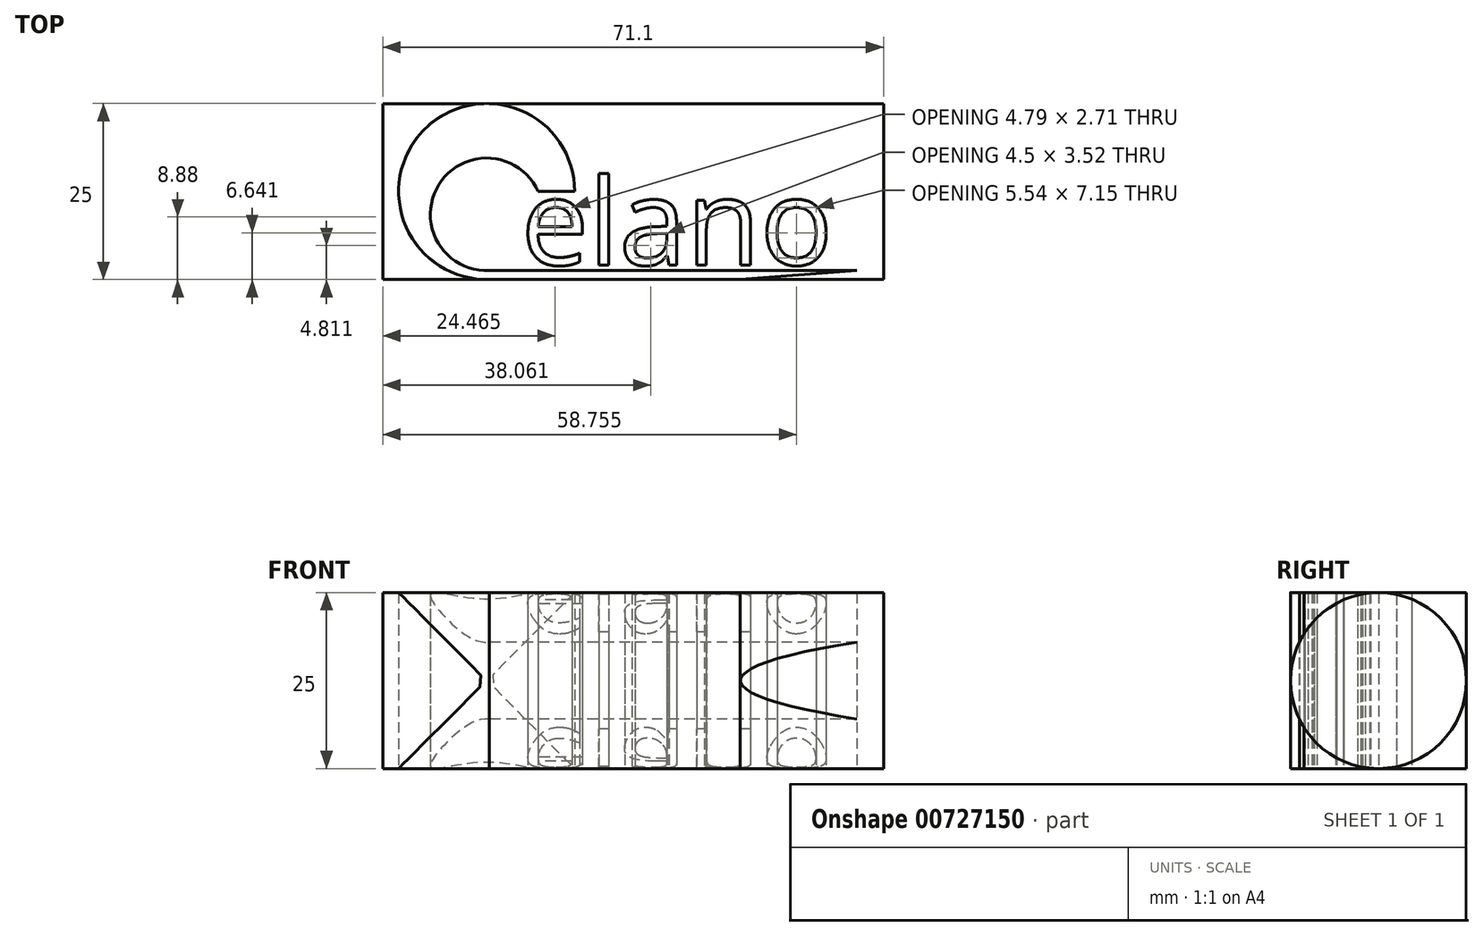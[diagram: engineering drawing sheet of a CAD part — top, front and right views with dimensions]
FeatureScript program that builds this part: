
annotation { "Feature Type Name" : "Feature", "Feature Type Description" : "" }
export const myFeature = defineFeature(function(context is Context, id is Id, definition is map)
    precondition{}
    {
        {
            var Q0;
            Q0=qCreatedBy(makeId("Top.planeOp"),FACE);
            var sketch = newSketch(context, id + "F0", { "sketchPlane" : qUnion([Q0])});
            skArc(sketch, "E0", {"start": v(-21.85, 0) * mm, "mid": v(-43.32, 8.7) * mm, "end": v(-33.99, -12.5) * mm});
            skLineSegment(sketch, "E1", {"start": v(-33.99, -12.5) * mm, "end": v(1.63, -12.5) * mm});
            skArc(sketch, "E2", {"start": v(-27.04, 0) * mm, "mid": v(-41.16, 0.95) * mm, "end": v(-33.99, -11.24) * mm});
            skLineSegment(sketch, "E3", {"start": v(-27.04, 0) * mm, "end": v(-21.85, 0) * mm});
            skLineSegment(sketch, "E4", {"start": v(-33.99, -11.24) * mm, "end": v(18.22, -11.24) * mm});
            skLineSegment(sketch, "E5", {"start": v(18.22, -11.24) * mm, "end": v(1.63, -12.5) * mm});
            skPoint(sketch, "E6.orphan", {"position": v(70.43, -11.24) * mm});
            skPoint(sketch, "E7.orphan", {"position": v(44.57, -12.5) * mm});
            skText(sketch, "E8", { "text": "elano", "fontName": "OpenSans-Regular.ttf"});
            const initialGuessF0  = {"E8": [-0.02946, -0.01043, 1, 0, 0.01232]};
            skSetInitialGuess(sketch, initialGuessF0);
            skSolve(sketch);
        }
        {
            var Q0;
            Q0 = qSketchRegion(id + "F0", true);
            extrude(context, id + "F1", {"entities" : qUnion([Q0]), "depth" : 25 * mm, "offsetDistance" : 25 * mm});
        }
        {
            var Q0;
            Q0=qCreatedBy(makeId("Right.planeOp"),FACE);
            var sketch = newSketch(context, id + "F2", { "sketchPlane" : qUnion([Q0])});
            skLineSegment(sketch, "E9", {"start": v(12.5, 25) * mm, "end": v(12.5, 0) * mm});
            skLineSegment(sketch, "E10.0", {"start": v(-12.5, 25) * mm, "end": v(12.5, 25) * mm});
            skLineSegment(sketch, "E11.0", {"start": v(-12.5, 25) * mm, "end": v(-12.5, 0) * mm});
            skLineSegment(sketch, "E12", {"start": v(-12.5, 0) * mm, "end": v(-12.5, 25) * mm});
            skCircle(sketch, "E13", {"center": v(0, 12.5) * mm, "radius": 12.5 * mm});
            skPoint(sketch, "E13.centerSnap0", {"position": v(-12.5, 12.5) * mm});
            skSolve(sketch);
        }
        {
            var Q0;
            Q0 = qSketchRegion(id + "F2", true);
            extrude(context, id + "F3", {"entities" : qUnion([Q0]), "depth" : 22 * mm, "offsetDistance" : 25 * mm, "hasSecondDirection" : true, "secondDirectionOppositeDirection" : true, "secondDirectionDepth" : 49.1 * mm});
        }
        {
            var Q0;
            Q0=makeQuery(id+"F3.opExtrude","SWEPT_BODY",BODY,{"disambiguationData":[OSD([sQuery(id+"F2.wireOp",EDGE,"E13")])]});
            var Q1;
            Q1=makeQuery(id+"F1.opExtrude","SWEPT_BODY",BODY,{"disambiguationData":[OSD([sQuery(id+"F0.wireOp",EDGE,"E8.sketch_text.stroke-67"),sQuery(id+"F0.wireOp",EDGE,"E8.sketch_text.stroke-68"),sQuery(id+"F0.wireOp",EDGE,"E8.sketch_text.stroke-69"),sQuery(id+"F0.wireOp",EDGE,"E8.sketch_text.stroke-70"),sQuery(id+"F0.wireOp",EDGE,"E8.sketch_text.stroke-71"),sQuery(id+"F0.wireOp",EDGE,"E8.sketch_text.stroke-72"),sQuery(id+"F0.wireOp",EDGE,"E8.sketch_text.stroke-73"),sQuery(id+"F0.wireOp",EDGE,"E8.sketch_text.stroke-74"),sQuery(id+"F0.wireOp",EDGE,"E8.sketch_text.stroke-75"),sQuery(id+"F0.wireOp",EDGE,"E8.sketch_text.stroke-76"),sQuery(id+"F0.wireOp",EDGE,"E8.sketch_text.stroke-77"),sQuery(id+"F0.wireOp",EDGE,"E8.sketch_text.stroke-78"),sQuery(id+"F0.wireOp",EDGE,"E8.sketch_text.stroke-79"),sQuery(id+"F0.wireOp",EDGE,"E8.sketch_text.stroke-80"),sQuery(id+"F0.wireOp",EDGE,"E8.sketch_text.stroke-81"),sQuery(id+"F0.wireOp",EDGE,"E8.sketch_text.stroke-82"),sQuery(id+"F0.wireOp",EDGE,"E8.sketch_text.stroke-83")])]});
            var Q2;
            Q2=makeQuery(id+"F1.opExtrude","SWEPT_BODY",BODY,{"disambiguationData":[OSD([sQuery(id+"F0.wireOp",EDGE,"E8.sketch_text.stroke-50"),sQuery(id+"F0.wireOp",EDGE,"E8.sketch_text.stroke-51"),sQuery(id+"F0.wireOp",EDGE,"E8.sketch_text.stroke-52"),sQuery(id+"F0.wireOp",EDGE,"E8.sketch_text.stroke-53"),sQuery(id+"F0.wireOp",EDGE,"E8.sketch_text.stroke-54"),sQuery(id+"F0.wireOp",EDGE,"E8.sketch_text.stroke-55"),sQuery(id+"F0.wireOp",EDGE,"E8.sketch_text.stroke-56"),sQuery(id+"F0.wireOp",EDGE,"E8.sketch_text.stroke-57"),sQuery(id+"F0.wireOp",EDGE,"E8.sketch_text.stroke-58"),sQuery(id+"F0.wireOp",EDGE,"E8.sketch_text.stroke-59"),sQuery(id+"F0.wireOp",EDGE,"E8.sketch_text.stroke-60"),sQuery(id+"F0.wireOp",EDGE,"E8.sketch_text.stroke-61"),sQuery(id+"F0.wireOp",EDGE,"E8.sketch_text.stroke-62"),sQuery(id+"F0.wireOp",EDGE,"E8.sketch_text.stroke-63"),sQuery(id+"F0.wireOp",EDGE,"E8.sketch_text.stroke-64"),sQuery(id+"F0.wireOp",EDGE,"E8.sketch_text.stroke-65"),sQuery(id+"F0.wireOp",EDGE,"E8.sketch_text.stroke-66")])]});
            var Q3;
            Q3=makeQuery(id+"F1.opExtrude","SWEPT_BODY",BODY,{"disambiguationData":[OSD([sQuery(id+"F0.wireOp",EDGE,"E8.sketch_text.stroke-23"),sQuery(id+"F0.wireOp",EDGE,"E8.sketch_text.stroke-24"),sQuery(id+"F0.wireOp",EDGE,"E8.sketch_text.stroke-25"),sQuery(id+"F0.wireOp",EDGE,"E8.sketch_text.stroke-26"),sQuery(id+"F0.wireOp",EDGE,"E8.sketch_text.stroke-27"),sQuery(id+"F0.wireOp",EDGE,"E8.sketch_text.stroke-28"),sQuery(id+"F0.wireOp",EDGE,"E8.sketch_text.stroke-29"),sQuery(id+"F0.wireOp",EDGE,"E8.sketch_text.stroke-30"),sQuery(id+"F0.wireOp",EDGE,"E8.sketch_text.stroke-31"),sQuery(id+"F0.wireOp",EDGE,"E8.sketch_text.stroke-32"),sQuery(id+"F0.wireOp",EDGE,"E8.sketch_text.stroke-33"),sQuery(id+"F0.wireOp",EDGE,"E8.sketch_text.stroke-34"),sQuery(id+"F0.wireOp",EDGE,"E8.sketch_text.stroke-35"),sQuery(id+"F0.wireOp",EDGE,"E8.sketch_text.stroke-36"),sQuery(id+"F0.wireOp",EDGE,"E8.sketch_text.stroke-37"),sQuery(id+"F0.wireOp",EDGE,"E8.sketch_text.stroke-38"),sQuery(id+"F0.wireOp",EDGE,"E8.sketch_text.stroke-39"),sQuery(id+"F0.wireOp",EDGE,"E8.sketch_text.stroke-40"),sQuery(id+"F0.wireOp",EDGE,"E8.sketch_text.stroke-41"),sQuery(id+"F0.wireOp",EDGE,"E8.sketch_text.stroke-42"),sQuery(id+"F0.wireOp",EDGE,"E8.sketch_text.stroke-43"),sQuery(id+"F0.wireOp",EDGE,"E8.sketch_text.stroke-44"),sQuery(id+"F0.wireOp",EDGE,"E8.sketch_text.stroke-45"),sQuery(id+"F0.wireOp",EDGE,"E8.sketch_text.stroke-46"),sQuery(id+"F0.wireOp",EDGE,"E8.sketch_text.stroke-47"),sQuery(id+"F0.wireOp",EDGE,"E8.sketch_text.stroke-48"),sQuery(id+"F0.wireOp",EDGE,"E8.sketch_text.stroke-49")])]});
            var Q4;
            Q4=makeQuery(id+"F1.opExtrude","SWEPT_BODY",BODY,{"disambiguationData":[OSD([sQuery(id+"F0.wireOp",EDGE,"E8.sketch_text.stroke-0"),sQuery(id+"F0.wireOp",EDGE,"E8.sketch_text.stroke-1"),sQuery(id+"F0.wireOp",EDGE,"E8.sketch_text.stroke-2"),sQuery(id+"F0.wireOp",EDGE,"E8.sketch_text.stroke-3"),sQuery(id+"F0.wireOp",EDGE,"E8.sketch_text.stroke-4"),sQuery(id+"F0.wireOp",EDGE,"E8.sketch_text.stroke-5"),sQuery(id+"F0.wireOp",EDGE,"E8.sketch_text.stroke-6"),sQuery(id+"F0.wireOp",EDGE,"E8.sketch_text.stroke-7"),sQuery(id+"F0.wireOp",EDGE,"E8.sketch_text.stroke-8"),sQuery(id+"F0.wireOp",EDGE,"E8.sketch_text.stroke-9"),sQuery(id+"F0.wireOp",EDGE,"E8.sketch_text.stroke-10"),sQuery(id+"F0.wireOp",EDGE,"E8.sketch_text.stroke-11"),sQuery(id+"F0.wireOp",EDGE,"E8.sketch_text.stroke-12"),sQuery(id+"F0.wireOp",EDGE,"E8.sketch_text.stroke-13"),sQuery(id+"F0.wireOp",EDGE,"E8.sketch_text.stroke-14"),sQuery(id+"F0.wireOp",EDGE,"E8.sketch_text.stroke-15"),sQuery(id+"F0.wireOp",EDGE,"E8.sketch_text.stroke-16"),sQuery(id+"F0.wireOp",EDGE,"E8.sketch_text.stroke-17"),sQuery(id+"F0.wireOp",EDGE,"E8.sketch_text.stroke-18")])]});
            var Q5;
            Q5=makeQuery(id+"F1.opExtrude","SWEPT_BODY",BODY,{"disambiguationData":[OSD([sQuery(id+"F0.wireOp",EDGE,"E0"),sQuery(id+"F0.wireOp",EDGE,"E1"),sQuery(id+"F0.wireOp",EDGE,"E2"),sQuery(id+"F0.wireOp",EDGE,"E3"),sQuery(id+"F0.wireOp",EDGE,"E4"),sQuery(id+"F0.wireOp",EDGE,"E5")])]});
            var Q6;
            Q6=makeQuery(id+"F1.opExtrude","SWEPT_BODY",BODY,{"disambiguationData":[OSD([sQuery(id+"F0.wireOp",EDGE,"E8.sketch_text.stroke-19"),sQuery(id+"F0.wireOp",EDGE,"E8.sketch_text.stroke-20"),sQuery(id+"F0.wireOp",EDGE,"E8.sketch_text.stroke-21"),sQuery(id+"F0.wireOp",EDGE,"E8.sketch_text.stroke-22")])]});
            booleanBodies(context, id + "F4", {"operationType" : BooleanOperationType.INTERSECTION, "tools" : qUnion([Q0, Q1, Q2, Q3, Q4, Q5, Q6]), "keepTools" : true});
        }
        {
            var Q0;
            Q0=makeQuery(id+"F3.opExtrude","SWEPT_BODY",BODY,{"disambiguationData":[OSD([sQuery(id+"F2.wireOp",EDGE,"E13")])]});
            var Q1;
            Q1=makeQuery(id+"F1.opExtrude","SWEPT_BODY",BODY,{"disambiguationData":[OSD([sQuery(id+"F0.wireOp",EDGE,"E0"),sQuery(id+"F0.wireOp",EDGE,"E1"),sQuery(id+"F0.wireOp",EDGE,"E2"),sQuery(id+"F0.wireOp",EDGE,"E3"),sQuery(id+"F0.wireOp",EDGE,"E4"),sQuery(id+"F0.wireOp",EDGE,"E5")])]});
            booleanBodies(context, id + "F5", {"operationType" : BooleanOperationType.INTERSECTION, "tools" : qUnion([Q0, Q1]), "keepTools" : true});
        }
        {
            var Q0;
            Q0=makeQuery(id+"F3.opExtrude","SWEPT_BODY",BODY,{"disambiguationData":[OSD([sQuery(id+"F2.wireOp",EDGE,"E13")])]});
            var Q1;
            Q1=makeQuery(id+"F1.opExtrude","SWEPT_BODY",BODY,{"disambiguationData":[OSD([sQuery(id+"F0.wireOp",EDGE,"E8.sketch_text.stroke-0"),sQuery(id+"F0.wireOp",EDGE,"E8.sketch_text.stroke-1"),sQuery(id+"F0.wireOp",EDGE,"E8.sketch_text.stroke-2"),sQuery(id+"F0.wireOp",EDGE,"E8.sketch_text.stroke-3"),sQuery(id+"F0.wireOp",EDGE,"E8.sketch_text.stroke-4"),sQuery(id+"F0.wireOp",EDGE,"E8.sketch_text.stroke-5"),sQuery(id+"F0.wireOp",EDGE,"E8.sketch_text.stroke-6"),sQuery(id+"F0.wireOp",EDGE,"E8.sketch_text.stroke-7"),sQuery(id+"F0.wireOp",EDGE,"E8.sketch_text.stroke-8"),sQuery(id+"F0.wireOp",EDGE,"E8.sketch_text.stroke-9"),sQuery(id+"F0.wireOp",EDGE,"E8.sketch_text.stroke-10"),sQuery(id+"F0.wireOp",EDGE,"E8.sketch_text.stroke-11"),sQuery(id+"F0.wireOp",EDGE,"E8.sketch_text.stroke-12"),sQuery(id+"F0.wireOp",EDGE,"E8.sketch_text.stroke-13"),sQuery(id+"F0.wireOp",EDGE,"E8.sketch_text.stroke-14"),sQuery(id+"F0.wireOp",EDGE,"E8.sketch_text.stroke-15"),sQuery(id+"F0.wireOp",EDGE,"E8.sketch_text.stroke-16"),sQuery(id+"F0.wireOp",EDGE,"E8.sketch_text.stroke-17"),sQuery(id+"F0.wireOp",EDGE,"E8.sketch_text.stroke-18")])]});
            booleanBodies(context, id + "F6", {"operationType" : BooleanOperationType.INTERSECTION, "tools" : qUnion([Q0, Q1]), "keepTools" : true});
        }
        {
            var Q0;
            Q0=makeQuery(id+"F3.opExtrude","SWEPT_BODY",BODY,{"disambiguationData":[OSD([sQuery(id+"F2.wireOp",EDGE,"E13")])]});
            var Q1;
            Q1=makeQuery(id+"F1.opExtrude","SWEPT_BODY",BODY,{"disambiguationData":[OSD([sQuery(id+"F0.wireOp",EDGE,"E8.sketch_text.stroke-19"),sQuery(id+"F0.wireOp",EDGE,"E8.sketch_text.stroke-20"),sQuery(id+"F0.wireOp",EDGE,"E8.sketch_text.stroke-21"),sQuery(id+"F0.wireOp",EDGE,"E8.sketch_text.stroke-22")])]});
            booleanBodies(context, id + "F7", {"operationType" : BooleanOperationType.INTERSECTION, "tools" : qUnion([Q0, Q1]), "keepTools" : true});
        }
        {
            var Q0;
            Q0=makeQuery(id+"F3.opExtrude","SWEPT_BODY",BODY,{"disambiguationData":[OSD([sQuery(id+"F2.wireOp",EDGE,"E13")])]});
            var Q1;
            Q1=makeQuery(id+"F1.opExtrude","SWEPT_BODY",BODY,{"disambiguationData":[OSD([sQuery(id+"F0.wireOp",EDGE,"E8.sketch_text.stroke-23"),sQuery(id+"F0.wireOp",EDGE,"E8.sketch_text.stroke-24"),sQuery(id+"F0.wireOp",EDGE,"E8.sketch_text.stroke-25"),sQuery(id+"F0.wireOp",EDGE,"E8.sketch_text.stroke-26"),sQuery(id+"F0.wireOp",EDGE,"E8.sketch_text.stroke-27"),sQuery(id+"F0.wireOp",EDGE,"E8.sketch_text.stroke-28"),sQuery(id+"F0.wireOp",EDGE,"E8.sketch_text.stroke-29"),sQuery(id+"F0.wireOp",EDGE,"E8.sketch_text.stroke-30"),sQuery(id+"F0.wireOp",EDGE,"E8.sketch_text.stroke-31"),sQuery(id+"F0.wireOp",EDGE,"E8.sketch_text.stroke-32"),sQuery(id+"F0.wireOp",EDGE,"E8.sketch_text.stroke-33"),sQuery(id+"F0.wireOp",EDGE,"E8.sketch_text.stroke-34"),sQuery(id+"F0.wireOp",EDGE,"E8.sketch_text.stroke-35"),sQuery(id+"F0.wireOp",EDGE,"E8.sketch_text.stroke-36"),sQuery(id+"F0.wireOp",EDGE,"E8.sketch_text.stroke-37"),sQuery(id+"F0.wireOp",EDGE,"E8.sketch_text.stroke-38"),sQuery(id+"F0.wireOp",EDGE,"E8.sketch_text.stroke-39"),sQuery(id+"F0.wireOp",EDGE,"E8.sketch_text.stroke-40"),sQuery(id+"F0.wireOp",EDGE,"E8.sketch_text.stroke-41"),sQuery(id+"F0.wireOp",EDGE,"E8.sketch_text.stroke-42"),sQuery(id+"F0.wireOp",EDGE,"E8.sketch_text.stroke-43"),sQuery(id+"F0.wireOp",EDGE,"E8.sketch_text.stroke-44"),sQuery(id+"F0.wireOp",EDGE,"E8.sketch_text.stroke-45"),sQuery(id+"F0.wireOp",EDGE,"E8.sketch_text.stroke-46"),sQuery(id+"F0.wireOp",EDGE,"E8.sketch_text.stroke-47"),sQuery(id+"F0.wireOp",EDGE,"E8.sketch_text.stroke-48"),sQuery(id+"F0.wireOp",EDGE,"E8.sketch_text.stroke-49")])]});
            booleanBodies(context, id + "F8", {"operationType" : BooleanOperationType.INTERSECTION, "tools" : qUnion([Q0, Q1]), "keepTools" : true});
        }
        {
            var Q0;
            Q0=makeQuery(id+"F3.opExtrude","SWEPT_BODY",BODY,{"disambiguationData":[OSD([sQuery(id+"F2.wireOp",EDGE,"E13")])]});
            var Q1;
            Q1=makeQuery(id+"F1.opExtrude","SWEPT_BODY",BODY,{"disambiguationData":[OSD([sQuery(id+"F0.wireOp",EDGE,"E8.sketch_text.stroke-50"),sQuery(id+"F0.wireOp",EDGE,"E8.sketch_text.stroke-51"),sQuery(id+"F0.wireOp",EDGE,"E8.sketch_text.stroke-52"),sQuery(id+"F0.wireOp",EDGE,"E8.sketch_text.stroke-53"),sQuery(id+"F0.wireOp",EDGE,"E8.sketch_text.stroke-54"),sQuery(id+"F0.wireOp",EDGE,"E8.sketch_text.stroke-55"),sQuery(id+"F0.wireOp",EDGE,"E8.sketch_text.stroke-56"),sQuery(id+"F0.wireOp",EDGE,"E8.sketch_text.stroke-57"),sQuery(id+"F0.wireOp",EDGE,"E8.sketch_text.stroke-58"),sQuery(id+"F0.wireOp",EDGE,"E8.sketch_text.stroke-59"),sQuery(id+"F0.wireOp",EDGE,"E8.sketch_text.stroke-60"),sQuery(id+"F0.wireOp",EDGE,"E8.sketch_text.stroke-61"),sQuery(id+"F0.wireOp",EDGE,"E8.sketch_text.stroke-62"),sQuery(id+"F0.wireOp",EDGE,"E8.sketch_text.stroke-63"),sQuery(id+"F0.wireOp",EDGE,"E8.sketch_text.stroke-64"),sQuery(id+"F0.wireOp",EDGE,"E8.sketch_text.stroke-65"),sQuery(id+"F0.wireOp",EDGE,"E8.sketch_text.stroke-66")])]});
            booleanBodies(context, id + "F9", {"operationType" : BooleanOperationType.INTERSECTION, "tools" : qUnion([Q0, Q1]), "keepTools" : true});
        }
        {
            var Q0;
            Q0=makeQuery(id+"F3.opExtrude","SWEPT_BODY",BODY,{"disambiguationData":[OSD([sQuery(id+"F2.wireOp",EDGE,"E13")])]});
            var Q1;
            Q1=makeQuery(id+"F1.opExtrude","SWEPT_BODY",BODY,{"disambiguationData":[OSD([sQuery(id+"F0.wireOp",EDGE,"E8.sketch_text.stroke-67"),sQuery(id+"F0.wireOp",EDGE,"E8.sketch_text.stroke-68"),sQuery(id+"F0.wireOp",EDGE,"E8.sketch_text.stroke-69"),sQuery(id+"F0.wireOp",EDGE,"E8.sketch_text.stroke-70"),sQuery(id+"F0.wireOp",EDGE,"E8.sketch_text.stroke-71"),sQuery(id+"F0.wireOp",EDGE,"E8.sketch_text.stroke-72"),sQuery(id+"F0.wireOp",EDGE,"E8.sketch_text.stroke-73"),sQuery(id+"F0.wireOp",EDGE,"E8.sketch_text.stroke-74"),sQuery(id+"F0.wireOp",EDGE,"E8.sketch_text.stroke-75"),sQuery(id+"F0.wireOp",EDGE,"E8.sketch_text.stroke-76"),sQuery(id+"F0.wireOp",EDGE,"E8.sketch_text.stroke-77"),sQuery(id+"F0.wireOp",EDGE,"E8.sketch_text.stroke-78"),sQuery(id+"F0.wireOp",EDGE,"E8.sketch_text.stroke-79"),sQuery(id+"F0.wireOp",EDGE,"E8.sketch_text.stroke-80"),sQuery(id+"F0.wireOp",EDGE,"E8.sketch_text.stroke-81"),sQuery(id+"F0.wireOp",EDGE,"E8.sketch_text.stroke-82"),sQuery(id+"F0.wireOp",EDGE,"E8.sketch_text.stroke-83")])]});
            booleanBodies(context, id + "F10", {"operationType" : BooleanOperationType.INTERSECTION, "tools" : qUnion([Q0, Q1]), "keepTools" : true});
        }
    });
